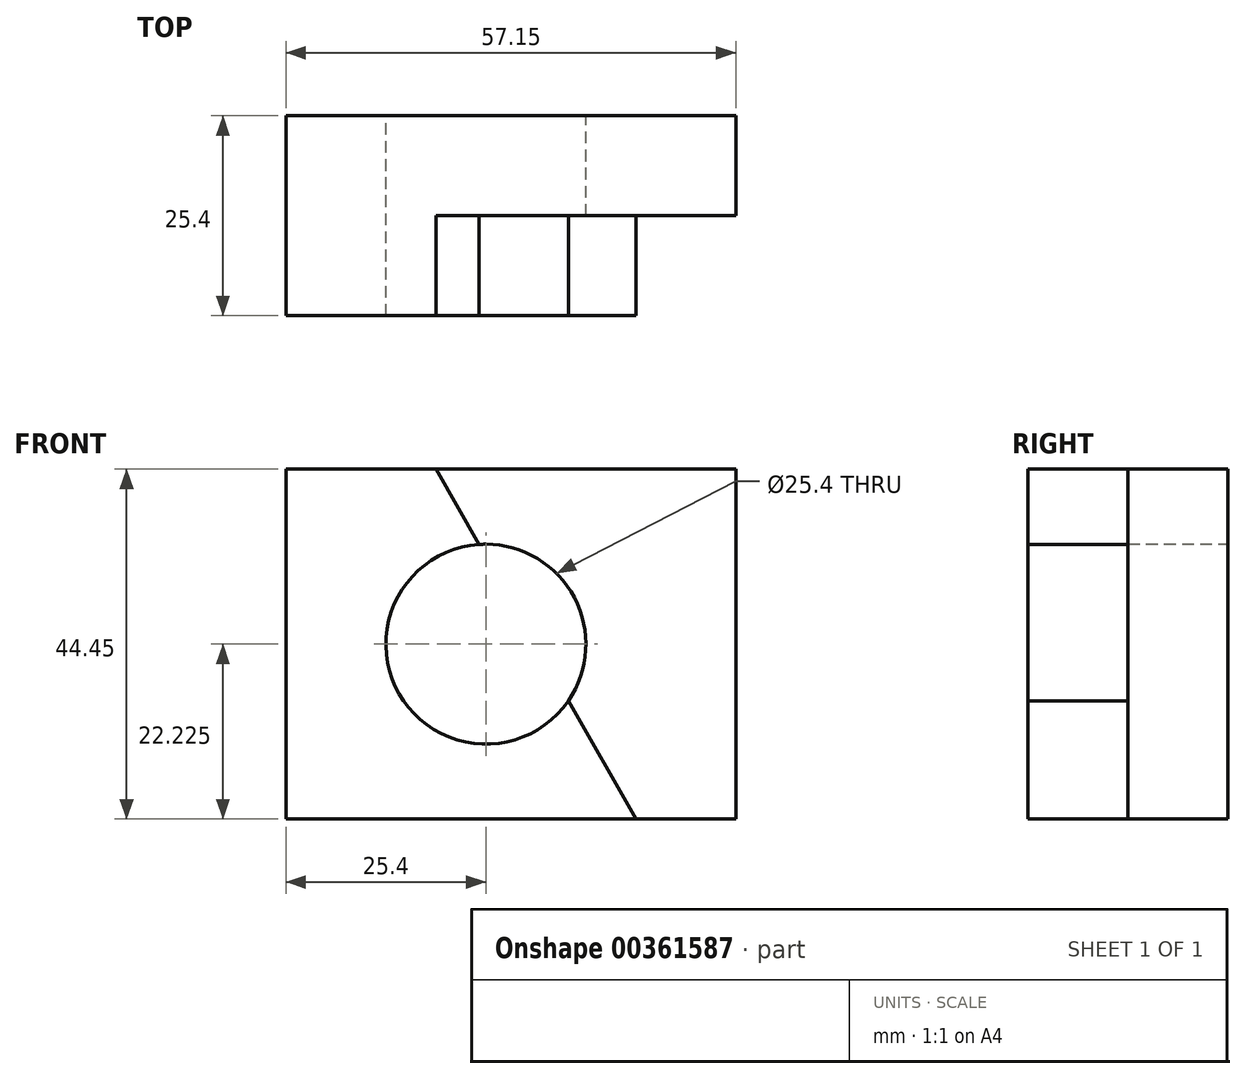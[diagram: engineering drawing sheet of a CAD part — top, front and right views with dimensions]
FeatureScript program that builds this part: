
annotation { "Feature Type Name" : "Feature", "Feature Type Description" : "" }
export const myFeature = defineFeature(function(context is Context, id is Id, definition is map)
    precondition{}
    {
        {
            var Q0;
            Q0=qCreatedBy(makeId("Front.planeOp"),FACE);
            var sketch = newSketch(context, id + "F0", { "sketchPlane" : qUnion([Q0])});
            skLineSegment(sketch, "E0", {"start": v(0, 0) * mm, "end": v(57.15, 0) * mm});
            skLineSegment(sketch, "E1", {"start": v(57.15, 0) * mm, "end": v(57.15, 44.45) * mm});
            skLineSegment(sketch, "E2", {"start": v(57.15, 44.45) * mm, "end": v(0, 44.45) * mm});
            skLineSegment(sketch, "E3", {"start": v(0, 44.45) * mm, "end": v(0, 0) * mm});
            skSolve(sketch);
        }
        {
            var Q0;
            Q0=makeQuery(id+"F0.imprint","IMPRINT",FACE,{"disambiguationData":[TD([[makeQuery(id+"F0.imprint","IMPRINT",EDGE,{"derivedFrom":sQuery(id+"F0.wireOp",EDGE,"E0")}),1.0]])]});
            extrude(context, id + "F1", {"entities" : qUnion([Q0]), "depth" : 25.4 * mm});
        }
        {
            var Q0;
            Q0=makeQuery(id+"F1.opExtrude","CAP_FACE",FACE,{"disambiguationData":[OSD([sQuery(id+"F0.wireOp",EDGE,"E0"),sQuery(id+"F0.wireOp",EDGE,"E1"),sQuery(id+"F0.wireOp",EDGE,"E2"),sQuery(id+"F0.wireOp",EDGE,"E3")])],"isStart":false});
            var sketch = newSketch(context, id + "F2", { "sketchPlane" : qUnion([Q0])});
            skLineSegment(sketch, "E4", {"start": v(19.05, 44.45) * mm, "end": v(44.45, 0) * mm});
            skSolve(sketch);
        }
        {
            var Q0;
            {var subQ0=sQuery(id+"F2.wireOp",EDGE,"E4");Q0=makeQuery(id+"F2.imprint","IMPRINT",FACE,{"disambiguationData":[TD([[makeQuery(id+"F2.imprint","IMPRINT",EDGE,{"derivedFrom":subQ0}),1.0]])]});}
            extrude(context, id + "F3", {"entities" : qUnion([Q0]), "operationType" : NewBodyOperationType.REMOVE, "oppositeDirection" : true, "depth" : 12.7 * mm});
        }
        {
            var Q0;
            Q0=makeQuery(id+"F1.opExtrude","CAP_FACE",FACE,{"disambiguationData":[OSD([sQuery(id+"F0.wireOp",EDGE,"E0"),sQuery(id+"F0.wireOp",EDGE,"E1"),sQuery(id+"F0.wireOp",EDGE,"E2"),sQuery(id+"F0.wireOp",EDGE,"E3")])],"isStart":true});
            var sketch = newSketch(context, id + "F4", { "sketchPlane" : qUnion([Q0])});
            skCircle(sketch, "E5", {"center": v(-25.4, 22.23) * mm, "radius": 12.7 * mm});
            skSolve(sketch);
        }
        {
            var Q0;
            Q0=makeQuery(id+"F4.imprint","IMPRINT",FACE,{"disambiguationData":[TD([[makeQuery(id+"F4.imprint","IMPRINT",EDGE,{"derivedFrom":sQuery(id+"F4.wireOp",EDGE,"E5")}),1.0]])]});
            extrude(context, id + "F5", {"entities" : qUnion([Q0]), "operationType" : NewBodyOperationType.REMOVE, "oppositeDirection" : true, "depth" : 25.4 * mm});
        }
    });
